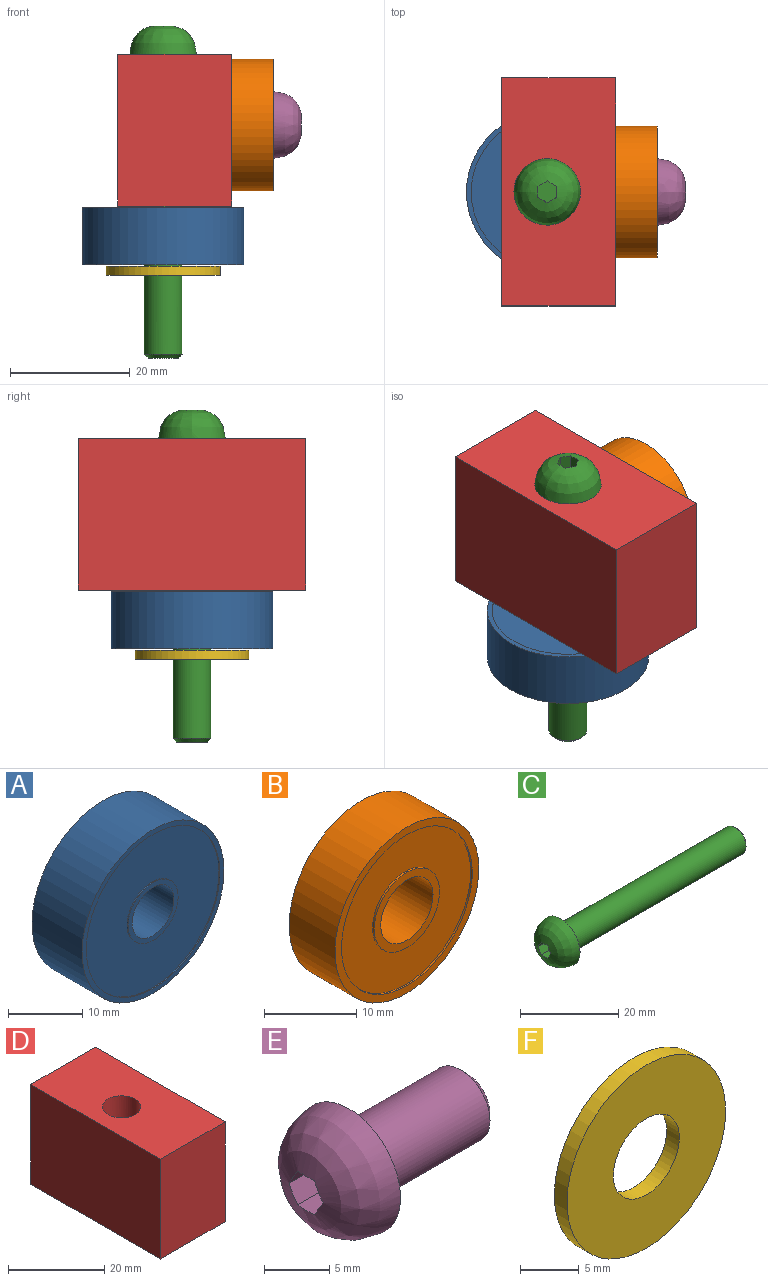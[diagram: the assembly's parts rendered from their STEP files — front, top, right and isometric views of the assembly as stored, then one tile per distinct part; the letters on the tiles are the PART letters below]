
ASSEMBLY  parts=6 mates=5
PART A: 12 faces, bbox 27x9.5x27 mm
  f0: cylinder r=4.76mm len=9.53mm, axis (0,1,0), area 5.7mm2, adj f4,f11
  f1: cylinder r=3.97mm len=9.53mm, axis (0,1,0), area 237.5mm2, adj f3,f4
  f2: cylinder r=4.76mm len=9.53mm, axis (0,1,0), area 5.7mm2, adj f3,f10
  f3: plane 9.53x9.53mm, normal (0,-1,0), area 21.8mm2, adj f1,f2
  f4: plane 9.53x9.53mm, normal (0,1,0), area 21.8mm2, adj f0,f1
  f5: cylinder r=12.7mm len=25.4mm, axis (0,1,0), area 15.2mm2, adj f9,f11
  f6: cylinder r=12.7mm len=25.4mm, axis (0,1,0), area 15.2mm2, adj f8,f10
  f7: cylinder r=13.49mm len=26.99mm, axis (0,1,0), area 807.6mm2, adj f8,f9
  f8: plane 26.99x26.99mm, normal (0,-1,0), area 65.3mm2, adj f6,f7
  f9: plane 26.99x26.99mm, normal (0,1,0), area 65.3mm2, adj f5,f7
  f10: plane 25.4x25.4mm, normal (0,-1,0), area 435.5mm2, adj f2,f6
  f11: plane 25.4x25.4mm, normal (0,1,0), area 435.5mm2, adj f0,f5
PART B: 12 faces, bbox 22x7x22 mm
  f0: cylinder r=5mm len=10mm, axis (0,1,0), area 7.9mm2, adj f4,f11
  f1: cylinder r=4mm len=8mm, axis (0,1,0), area 175.9mm2, adj f3,f4
  f2: cylinder r=5mm len=10mm, axis (0,1,0), area 7.9mm2, adj f3,f10
  f3: plane 10x10mm, normal (0,-1,0), area 28.3mm2, adj f1,f2
  f4: plane 10x10mm, normal (0,1,0), area 28.3mm2, adj f0,f1
  f5: cylinder r=10mm len=20mm, axis (0,1,0), area 15.7mm2, adj f9,f11
  f6: cylinder r=10mm len=20mm, axis (0,1,0), area 15.7mm2, adj f8,f10
  f7: cylinder r=11mm len=22mm, axis (0,1,0), area 483.8mm2, adj f8,f9
  f8: plane 22x22mm, normal (0,-1,0), area 66mm2, adj f6,f7
  f9: plane 22x22mm, normal (0,1,0), area 66mm2, adj f5,f7
  f10: plane 20x20mm, normal (0,-1,0), area 235.6mm2, adj f2,f6
  f11: plane 20x20mm, normal (0,1,0), area 235.6mm2, adj f0,f5
PART C: 12 faces, bbox 56.1x11.6x11.6 mm
  f0: plane 11.12x11.12mm, normal (1,0,0), area 65.3mm2, adj f2,f10
  f1: plane 5.08x5.08mm, normal (1,0,0), area 20.3mm2, adj f11
  f2: cylinder r=3.17mm len=50.17mm, axis (1,0,0), area 1000.7mm2, adj f0,f11
  f3: plane 3.62x2.33mm, normal (0,0,-1), area 5.7mm2, adj f4,f8,f9,f10
  f4: plane 3.62x2.08mm, normal (0,-0.87,-0.5), area 5.7mm2, adj f3,f5,f9,f10
  f5: plane 3.62x2.08mm, normal (0,-0.87,0.5), area 5.7mm2, adj f4,f6,f9,f10
  f6: plane 3.24x1.97mm, normal (0,0,1), area 5.7mm2, adj f5,f7,f9,f10
  f7: plane 3.62x2.08mm, normal (0,0.87,0.5), area 5.7mm2, adj f6,f8,f9,f10
  f8: plane 3.62x2.08mm, normal (0,0.87,-0.5), area 5.7mm2, adj f3,f7,f9,f10
  f9: plane 3.67x3.18mm, normal (-1,0,0), area 8.7mm2, adj f3,f4,f5,f6,f7,f8
  f10: bspline ~11.11x11.11mm, area 174.9mm2, adj f0,f3,f4,f5,f6,f7,f8
  f11: cone r=2.54mm half-angle=45deg, axis (-1,0,0), area 16.1mm2, adj f1,f2
PART D: 8 faces, bbox 19.1x38.1x25.4 mm
  f0: plane 38.1x25.4mm, normal (-1,0,0), area 967.7mm2, adj f1,f3,f4,f5
  f1: plane 38.1x19.05mm, normal (0,0,-1), area 676.3mm2, adj f0,f2,f4,f5,f6
  f2: plane 38.1x25.4mm, normal (1,0,0), area 918.3mm2, adj f1,f3,f4,f5,f7
  f3: plane 38.1x19.05mm, normal (0,0,1), area 676.3mm2, adj f0,f2,f4,f5,f6
  f4: plane 25.4x19.05mm, normal (0,-1,0), area 483.9mm2, adj f0,f1,f2,f3
  f5: plane 25.4x19.05mm, normal (0,1,0), area 483.9mm2, adj f0,f1,f2,f3
  f6: cylinder r=3.97mm len=25.4mm, axis (0,0,-1), area 570.4mm2, adj f1,f3,f7
  f7: cylinder r=3.97mm len=11.43mm, axis (1,0,0), area 222mm2, adj f2,f6
PART E: 12 faces, bbox 18x11.6x11.6 mm
  f0: plane 11.12x11.12mm, normal (1,0,0), area 65.3mm2, adj f2,f10
  f1: plane 5.08x5.08mm, normal (1,0,0), area 20.3mm2, adj f11
  f2: cylinder r=3.17mm len=12.07mm, axis (1,0,0), area 240.7mm2, adj f0,f11
  f3: plane 3.62x2.33mm, normal (0,0,-1), area 5.7mm2, adj f4,f8,f9,f10
  f4: plane 3.62x2.08mm, normal (0,-0.87,-0.5), area 5.7mm2, adj f3,f5,f9,f10
  f5: plane 3.62x2.08mm, normal (0,-0.87,0.5), area 5.7mm2, adj f4,f6,f9,f10
  f6: plane 3.24x1.97mm, normal (0,0,1), area 5.7mm2, adj f5,f7,f9,f10
  f7: plane 3.62x2.08mm, normal (0,0.87,0.5), area 5.7mm2, adj f6,f8,f9,f10
  f8: plane 3.62x2.08mm, normal (0,0.87,-0.5), area 5.7mm2, adj f3,f7,f9,f10
  f9: plane 3.67x3.18mm, normal (-1,0,0), area 8.7mm2, adj f3,f4,f5,f6,f7,f8
  f10: bspline ~11.11x11.11mm, area 174.9mm2, adj f0,f3,f4,f5,f6,f7,f8
  f11: cone r=2.54mm half-angle=45deg, axis (-1,0,0), area 16.1mm2, adj f1,f2
PART F: 4 faces, bbox 19.1x1.5x19.1 mm
  f0: cylinder r=3.97mm len=7.94mm, axis (0,1,0), area 38mm2, adj f2,f3
  f1: cylinder r=9.53mm len=19.05mm, axis (0,1,0), area 91.2mm2, adj f2,f3
  f2: plane 19.05x19.05mm, normal (0,-1,0), area 235.5mm2, adj f0,f1
  f3: plane 19.05x19.05mm, normal (0,1,0), area 235.5mm2, adj f0,f1
PLACE A rot(axis=(0.38,0.65,0.65),138.1deg) t=(-11.43,-19.05,-5.08)mm
PLACE B rot(axis=(0.58,-0.58,0.58),120deg) t=(3.5,-19.05,13.54)mm
PLACE C rot(axis=(0,1,0),90deg) t=(-11.43,-19.05,-25.4)mm
PLACE D t=(-19.05,0,0)mm
PLACE E rot(axis=(0,-1,0),180deg) t=(-5.7,-19.05,13.54)mm
PLACE F rot(axis=(0.81,-0.42,-0.42),102.1deg) t=(-11.43,-19.05,-10.85)mm
MATE fastened B.f1 <-> D.f7  axis (-1,0,0) through (0,-19.05,13.54)mm
MATE fastened E.f11 <-> B.f1  axis (-1,0,0) through (7,-19.05,13.54)mm
MATE cylindrical A.f5 <-> F.f0  axis (0,0,1) through (-11.43,-19.05,-0.51)mm
MATE cylindrical A.f5 <-> C.f11  axis (0,0,-1) through (-11.43,-19.05,-9.65)mm
MATE fastened C.f11 <-> D.f6  axis (0,0,-1) through (-11.43,-19.05,25.4)mm
